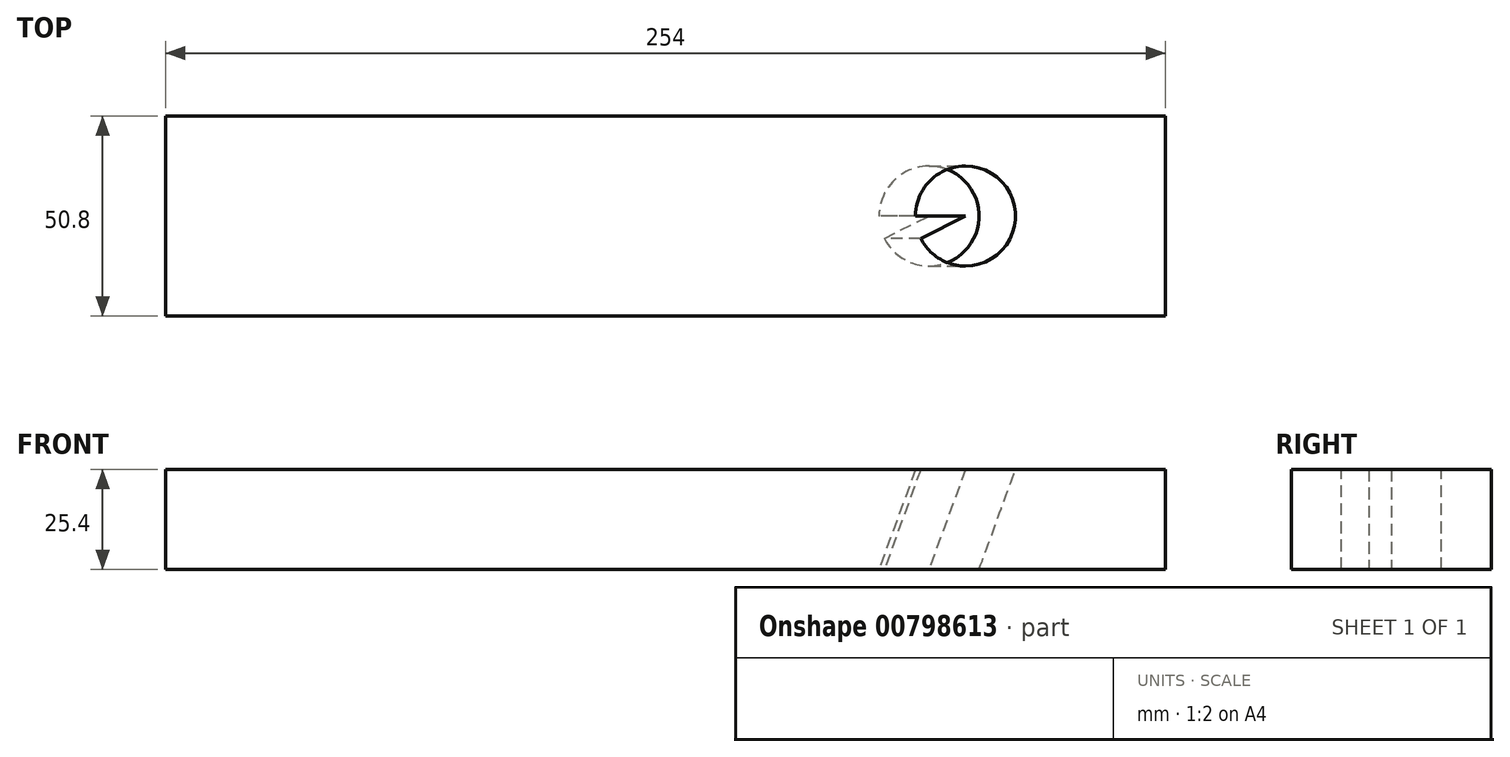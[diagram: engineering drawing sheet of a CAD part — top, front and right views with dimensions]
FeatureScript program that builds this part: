
annotation { "Feature Type Name" : "Feature", "Feature Type Description" : "" }
export const myFeature = defineFeature(function(context is Context, id is Id, definition is map)
    precondition{}
    {
        {
            var Q0;
            Q0=qCreatedBy(makeId("Top.planeOp"),FACE);
            var sketch = newSketch(context, id + "F0", { "sketchPlane" : qUnion([Q0])});
            skLineSegment(sketch, "E0.bottom", {"start": v(127, -25.4) * mm, "end": v(-127, -25.4) * mm});
            skLineSegment(sketch, "E0.top", {"start": v(127, 25.4) * mm, "end": v(-127, 25.4) * mm});
            skLineSegment(sketch, "E0.left", {"start": v(127, -25.4) * mm, "end": v(127, 25.4) * mm});
            skLineSegment(sketch, "E0.right", {"start": v(-127, -25.4) * mm, "end": v(-127, 25.4) * mm});
            skPoint(sketch, "E0.middle", {"position": v(0, 0) * mm});
            skSolve(sketch);
        }
        {
            var Q0;
            Q0=makeQuery(id+"F0.imprint","IMPRINT",FACE,{"disambiguationData":[TD([[makeQuery(id+"F0.imprint","IMPRINT",EDGE,{"derivedFrom":sQuery(id+"F0.wireOp",EDGE,"E0.bottom")}),-1.0]])]});
            extrude(context, id + "F1", {"entities" : qUnion([Q0]), "depth" : 25.4 * mm, "offsetDistance" : 25.4 * mm});
        }
        {
            var Q0;
            Q0=makeQuery(id+"F1.opExtrude","CAP_FACE",FACE,{"disambiguationData":[OSD([sQuery(id+"F0.wireOp",EDGE,"E0.bottom"),sQuery(id+"F0.wireOp",EDGE,"E0.top"),sQuery(id+"F0.wireOp",EDGE,"E0.left"),sQuery(id+"F0.wireOp",EDGE,"E0.right")])],"isStart":false});
            var sketch = newSketch(context, id + "F2", { "sketchPlane" : qUnion([Q0])});
            skLineSegment(sketch, "E1", {"start": v(127, -25.4) * mm, "end": v(25.4, 25.4) * mm});
            skLineSegment(sketch, "E2", {"start": v(25.4, 25.4) * mm, "end": v(25.4, -25.4) * mm});
            skLineSegment(sketch, "E3", {"start": v(25.4, -25.4) * mm, "end": v(127, 25.4) * mm});
            skLineSegment(sketch, "E4", {"start": v(127, 25.4) * mm, "end": v(127, 0) * mm});
            skLineSegment(sketch, "E5", {"start": v(127, 0) * mm, "end": v(25.4, 0) * mm});
            skLineSegment(sketch, "E6", {"start": v(76.2, 0) * mm, "end": v(76.2, -25.4) * mm});
            skCircle(sketch, "E7", {"center": v(76.2, 0) * mm, "radius": 12.7 * mm});
            skSolve(sketch);
        }
        {
            var Q0;
            Q0=makeQuery(id+"F1.opExtrude","SWEPT_FACE",FACE,{"disambiguationData":[OSD([sQuery(id+"F0.wireOp",EDGE,"E0.bottom")])]});
            var sketch = newSketch(context, id + "F3", { "sketchPlane" : qUnion([Q0])});
            skLineSegment(sketch, "E8", {"start": v(74.68, 0) * mm, "end": v(74.68, 25.4) * mm});
            skLineSegment(sketch, "E9", {"start": v(74.68, 25.4) * mm, "end": v(65.44, 0) * mm});
            skLineSegment(sketch, "E10", {"start": v(65.44, 0) * mm, "end": v(74.68, 0) * mm});
            skSolve(sketch);
        }
        {
            var Q0;
            {var subQ0=sQuery(id+"F2.wireOp",EDGE,"E7");var subQ1=sQuery(id+"F2.wireOp",EDGE,"E1");var subQ2=makeQuery(id+"F2.imprint","INTERSECT",VERTEX,{"disambiguationData":[OD(0.0)],"derivedFrom":[subQ1,subQ0]});Q0=makeQuery(id+"F2.imprint","IMPRINT",FACE,{"disambiguationData":[TD([[makeQuery(id+"F2.imprint","IMPRINT",EDGE,{"disambiguationData":[TD([[subQ2,1.0]])],"derivedFrom":subQ0}),1.0]])]});}
            var Q1;
            {var subQ0=sQuery(id+"F2.wireOp",EDGE,"E7");var subQ1=sQuery(id+"F2.wireOp",EDGE,"E1");var subQ2=makeQuery(id+"F2.imprint","INTERSECT",VERTEX,{"disambiguationData":[OD(0.0)],"derivedFrom":[subQ1,subQ0]});Q1=makeQuery(id+"F2.imprint","IMPRINT",FACE,{"disambiguationData":[TD([[makeQuery(id+"F2.imprint","IMPRINT",EDGE,{"disambiguationData":[TD([[subQ2,-1.0]])],"derivedFrom":subQ0}),1.0]])]});}
            var Q2;
            {var subQ0=sQuery(id+"F2.wireOp",EDGE,"E5");var subQ3=sQuery(id+"F2.wireOp",EDGE,"E7");var subQ5=makeQuery(id+"F2.imprint","INTERSECT",VERTEX,{"disambiguationData":[OD(0.0)],"derivedFrom":[subQ0,subQ3]});Q2=makeQuery(id+"F2.imprint","IMPRINT",FACE,{"disambiguationData":[TD([[makeQuery(id+"F2.imprint","IMPRINT",EDGE,{"disambiguationData":[TD([[subQ5,-1.0]])],"derivedFrom":subQ3}),1.0]])]});}
            var Q3;
            {var subQ0=sQuery(id+"F2.wireOp",EDGE,"E6");var subQ3=sQuery(id+"F2.wireOp",EDGE,"E7");var subQ5=makeQuery(id+"F2.imprint","INTERSECT",VERTEX,{"derivedFrom":[subQ0,subQ3]});Q3=makeQuery(id+"F2.imprint","IMPRINT",FACE,{"disambiguationData":[TD([[makeQuery(id+"F2.imprint","IMPRINT",EDGE,{"disambiguationData":[TD([[subQ5,1.0]])],"derivedFrom":subQ3}),1.0]])]});}
            var Q4;
            {var subQ0=sQuery(id+"F2.wireOp",EDGE,"E6");var subQ3=sQuery(id+"F2.wireOp",EDGE,"E7");var subQ5=makeQuery(id+"F2.imprint","INTERSECT",VERTEX,{"derivedFrom":[subQ0,subQ3]});Q4=makeQuery(id+"F2.imprint","IMPRINT",FACE,{"disambiguationData":[TD([[makeQuery(id+"F2.imprint","IMPRINT",EDGE,{"disambiguationData":[TD([[subQ5,-1.0]])],"derivedFrom":subQ3}),1.0]])]});}
            var Q5;
            {var subQ1=sQuery(id+"F2.wireOp",EDGE,"E1");var subQ3=sQuery(id+"F2.wireOp",EDGE,"E7");var subQ4=makeQuery(id+"F2.imprint","INTERSECT",VERTEX,{"disambiguationData":[OD(1.0)],"derivedFrom":[subQ1,subQ3]});Q5=makeQuery(id+"F2.imprint","IMPRINT",FACE,{"disambiguationData":[TD([[makeQuery(id+"F2.imprint","IMPRINT",EDGE,{"disambiguationData":[TD([[subQ4,-1.0]])],"derivedFrom":subQ3}),1.0]])]});}
            var Q6;
            {var subQ1=sQuery(id+"F2.wireOp",EDGE,"E3");var subQ3=sQuery(id+"F2.wireOp",EDGE,"E7");var subQ4=makeQuery(id+"F2.imprint","INTERSECT",VERTEX,{"disambiguationData":[OD(0.0)],"derivedFrom":[subQ1,subQ3]});Q6=makeQuery(id+"F2.imprint","IMPRINT",FACE,{"disambiguationData":[TD([[makeQuery(id+"F2.imprint","IMPRINT",EDGE,{"disambiguationData":[TD([[subQ4,1.0]])],"derivedFrom":subQ3}),1.0]])]});}
            var Q7;
            Q7=sQuery(id+"F3.wireOp",EDGE,"E9");
            sweep(context, id + "F4", {"operationType" : NewBodyOperationType.REMOVE, "profiles" : qUnion([Q0, Q1, Q2, Q3, Q4, Q5, Q6]), "path" : qUnion([Q7])});
        }
    });
